# Revit family: Grohe_SinkMixer_Essence_30503KF0
name_source: partatom
category: Plumbing Fixtures
units: mm (PartAtom-declared; Revit-internal decimal feet)

## family parameters
Cut with Voids When Loaded = No
Host = Face
OmniClass Number = 23.45.05.00
OmniClass Title = Sanitary Equipment
Part Type = Normal
Room Calculation Point = No
Round Connector Dimension = Use Diameter
Shared = No

## types (1)
- ESSENCE Sink Mixer (30503KF0)
    Assembly Code = D2010
    AssetType = Fixed
    BIMObjectName = Grohe_SinkMixer_Essence_30503KF0
    CO2NeutralProduction = GROHE is one of the first leading manufacturer within the sanitary industry having a CO2-neutral production.
    CW Connection = Yes
    ClassificationName = Uniclass2015
    ClassificationValue = Pr_40_20_87_55
    Color = Matt Black
    Cost = 0 $
    Default Elevation = 0 mm  [stored 0 ft]
    Description = ESSENCE Sink Mixer
    DimensionsDocumentLink = https://cdn.cloud.grohe.com
    DocumentationCertificates = https://www.bimstore.co
    DocumentationInstallationGuide = https://www.bimstore.co
    DocumentationLiterature = https://www.bimstore.co
    DocumentationMaintenance = https://www.bimstore.co
    DocumentationTechnical = https://www.bimstore.co
    DurationUnit = Years
    EF000003 = Top/tap hole
    EF000139 = Other
    EF001707 = 70 °C
    EF002149 = TRUE
    EF002286 = Hose (gland nut)
    EF002671 = Black
    EF007955 = FALSE
    EF011775 = not applicable
    EF011779 = FALSE
    EF011781 = not applicable
    EF012753 = 8.0
    EF014578 = not applicable
    EF014591 = FALSE
    EF016731 = Group I,<= 20 dB(A)
    EF020105 = No
    EF020780 = Single-grip
    EF020781 = Cartouche, ceramic
    EF020785 = 3/8 inch
    EF020787 = Group II, <=30 dB(A)
    EF020789 = 240 mm  [stored 0.787402 ft]
    EF020791 = Brass
    EF020792 = FALSE
    EF020795 = Flexible with rinsing shower
    EF020796 = 530 mm  [stored 1.73885 ft]
    EF020797 = 197 mm
    EF020799 = TRUE
    EF020800 = FALSE
    EF020801 = FALSE
    EF020803 = FALSE
    EF020804 = FALSE
    EF020871 = TRUE
    EF020872 = TRUE
    EF020873 = FALSE
    EF021652 = FALSE
    EF021758 = TRUE
    EF021808 = 1-hole
    EF021835 = 0 mm  [stored 0 ft]
    EF022042 = Z
    EF022750 = Other
    EF023686 = not applicable
    EF023687 = FALSE
    EF023688 = Foam jet nozzle
    EF023957 = TRUE
    EF025109 = Other
    EF025247 = FALSE
    EFDE0022 = Group I, <=20 dB(A)
    EFSE0002 = TRUE
    Ecojoy = No
    ExpectedLife = 0
    FullRecyclabilityOfPlastic = All plastic components are fully recyclable
    GROHESocialCommittment = green.grohe.com/social_engagement
    GROHESustainability = green.grohe.com
    HW Connection = Yes
    IfcExportAs = IfcPipeFitting
    IfcExportType = IfcPipeFittingType
    Keynote = N13
    Manufacturer = Grohe
    ManufacturerName = Grohe
    Model = ESSENCE Sink Mixer
    ModelNumber = 30503KF0
    ModelReference = ESSENCE Sink Mixer
    NBSDescription = Mixer taps
    NBSObjectName = Grohe - Mixer taps
    NBSReference = 45-35-70/345
    NominalDepth = 0 mm  [stored 0 ft]
    NominalHeight = 0 mm  [stored 0 ft]
    NominalLength = 0 mm  [stored 0 ft]
    PQDiagramLink = https://cdn.cloud.grohe.com
    PrimaryMaterial = Grohe_MattBlack
    ProductDescription = single hole installation

GROHE Long-Life Shine finish

GROHE SilkMove 28 mm ceramic cartridge

flow straightener

with integrated temperature limiter

professional spray

with flexible, hygienic GROHFlexx kitchen santoprene hose

diverter: laminar spray/SpeedClean shower jet

automatic return to laminar spray

metal spray

GROHE Magnetic Docking guarantees easy retraction and smooth docking of the spray head back to the starting position

swivel spout, swivel area 360°

protected against backflow

flexible connection hoses

metal fixation set

professional exclusive
    ProductNumber = 30503KF0
    ProductPageURL = https://www.grohe.co.uk
    ProductShortText = Essence Single-lever sink mixer 1/2"
    ProductType = Single Lever Mixer
    ProductionYear = 2023
    SustainabilityAward = green.grohe.com/awards
    SustainabilityReport = green.grohe.com/reporting
    Type Comments = ESSENCE Sink Mixer
    TypeName = ESSENCE Sink Mixer
    URL = https://www.grohe.co.uk
    Vent Connection = No
    WarrantyDurationLabor = 0
    WarrantyDurationParts = 0
    WarrantyDurationUnit = Years
    Waste Connection = No
    _BSBibleVersion = 17
    _BimSpecGuid = 0
    _CurrentRevision = 1
    _DistributedBy = https://www.bimstore.co
    _ObjectUserGuide = https://www.bimstore.co

note: [stored X ft] marks values corroborated as IEEE doubles in the binary element streams (Revit-internal decimal feet)

## geometry (parser evidence)
native form markers: Sweep x1
no freeform markers — native parametric forms only
